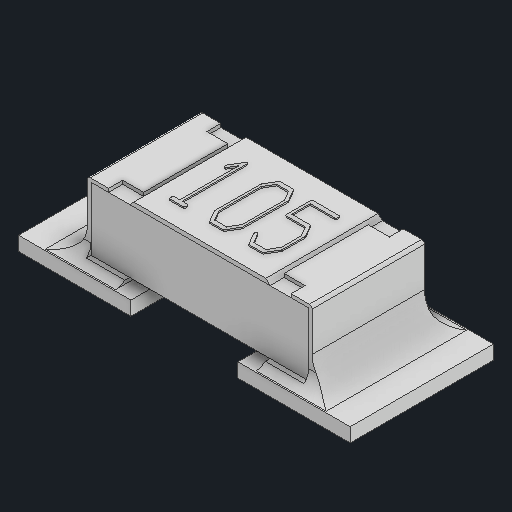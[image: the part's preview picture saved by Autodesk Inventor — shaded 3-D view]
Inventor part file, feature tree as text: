
AUTODESK INVENTOR PART (.ipt)
format: ipt  version: 2023 (Build 270158000, 158)  size: 219,648 bytes
history: native  units: in
note: dims shown in document units (in); Inventor stores cm internally (conversion verified against a paired STEP export)
features: other x2, fillet x2
ambient origin geometry x8: Origin, YZ Plane, XZ Plane, XY Plane, X Axis, Y Axis, Z Axis, Center Point
bodies: Solid1 (feature_tree), Solid2 (feature_tree), Solid3 (feature_tree), Solid4 (feature_tree)
feature tree (4):
  other  "Boss-Extrude1"
  other  "Boss-Extrude4"
  fillet  "Fillet6"  [1 undecoded]
  fillet  "Fillet5"  [1 undecoded]
note: 2 required parameter values undecoded (feature->parameter linkage not recoverable at this tier; creation-order binding heuristic only, values carry confidence <= 0.55)
